# Revit family: NLRS_57_AIR_UN_Swirl-diffuser-rtfoca-suppy_LT_sacs
name_source: partatom
category: Air Terminals
units: mm (PartAtom-declared; Revit-internal decimal feet)

## family parameters
Always vertical = Yes
Cut with Voids When Loaded = No
Part Type = Normal
Room Calculation Point = Yes
Round Connector Dimension = Use Diameter
Shared = No
Work Plane-Based = No

## types (5) — shared parameters
Assembly Code = 57.00
Description = Round flanged Swirl supply grill, Type RTFOC
IfcDescription = Round flanged Swirl supply grill, Type RTFOC
IfcExportAs = IfcAirterminal
IfcExportType = Diffuser
Manufacturer = Solid Air Climate Solutions
NLRS_C_content_datum_uitgifte = 26-05-2025
NLRS_C_content_provider = Solid Air Climate Solutions
NLRS_C_content_versie = 4.22.00
NLRS_C_description = Round flanged Swirl supply grill, Type RTFOC
SACS_Data_Hidden = RTFOCA_Data
SACS_Data_Hidden2 = RTFO_Factors
SACS_W_Correction_Factor = 1
URL = https://solid-air.nl
zero-valued in all types: Default Elevation

## per-type parameters (varying)
| type | Max Flow | Min Flow | SACS_Base_Index | SACS_Connecter_Height_Offset | SACS_Diameter | SACS_Diameter2 | SACS_Factor_LpF1 | SACS_Factor_LpF2 | SACS_Factor_PsF1 | SACS_Factor_PsF2 | SACS_Factor_WF1 | SACS_Factor_WF2 | SACS_Logo_X | SACS_Offset1 | SACS_Offset2 |
| 125 | 288.0 m³/h | 72.0 m³/h | 1 | 55 mm  [stored 0.180446 ft] | 123 mm  [stored 0.403543 ft] | 124 mm  [stored 0.406824 ft] | -115.154705 | 30.428942 | 0.002805 | 2.050375 | 0.011179 | 1.033159 | 74.5 mm  [stored 0.244423 ft] | 22 mm  [stored 0.0721785 ft] | 35 mm  [stored 0.114829 ft] |
| 160 | 450.0 m³/h | 108.0 m³/h | 2 | 80 mm  [stored 0.262467 ft] | 158 mm | 158 mm | -131.442504 | 30.452739 | 0.001165 | 1.973171 | 0.01185 | 0.966729 | 92 mm  [stored 0.301837 ft] | 27 mm  [stored 0.0885827 ft] | 35 mm  [stored 0.114829 ft] |
| 200 | 720.0 m³/h | 180.0 m³/h | 3 | 95 mm | 198 mm  [stored 0.649606 ft] | 198 mm  [stored 0.649606 ft] | -143.977422 | 30.747193 | 0.000218 | 2.047352 | 0.009517 | 0.963131 | 112 mm  [stored 0.367454 ft] | 32 mm  [stored 0.104987 ft] | 45 mm  [stored 0.147638 ft] |
| 250 | 900.0 m³/h | 288.0 m³/h | 4 | 115 mm  [stored 0.377297 ft] | 248 mm  [stored 0.813648 ft] | 249 mm  [stored 0.816929 ft] | -155.042399 | 30.404139 | 0.000141 | 1.970253 | 0.007167 | 0.973105 | 137 mm  [stored 0.449475 ft] | 42 mm  [stored 0.137795 ft] | 55 mm  [stored 0.180446 ft] |
| 315 | 900.0 m³/h | 288.0 m³/h | 5 | 120 mm  [stored 0.393701 ft] | 313 mm  [stored 1.0269 ft] | 313.5 mm  [stored 1.02854 ft] | -166.716478 | 30.147475 | 3.8e-05 | 2.025389 | 0.005126 | 0.988195 | 169.5 mm  [stored 0.556102 ft] | 42 mm  [stored 0.137795 ft] | 55 mm  [stored 0.180446 ft] |

note: [stored X ft] marks values corroborated as IEEE doubles in the binary element streams (Revit-internal decimal feet)

## geometry (parser evidence)
native form markers: Sweep x13
no freeform markers — native parametric forms only
